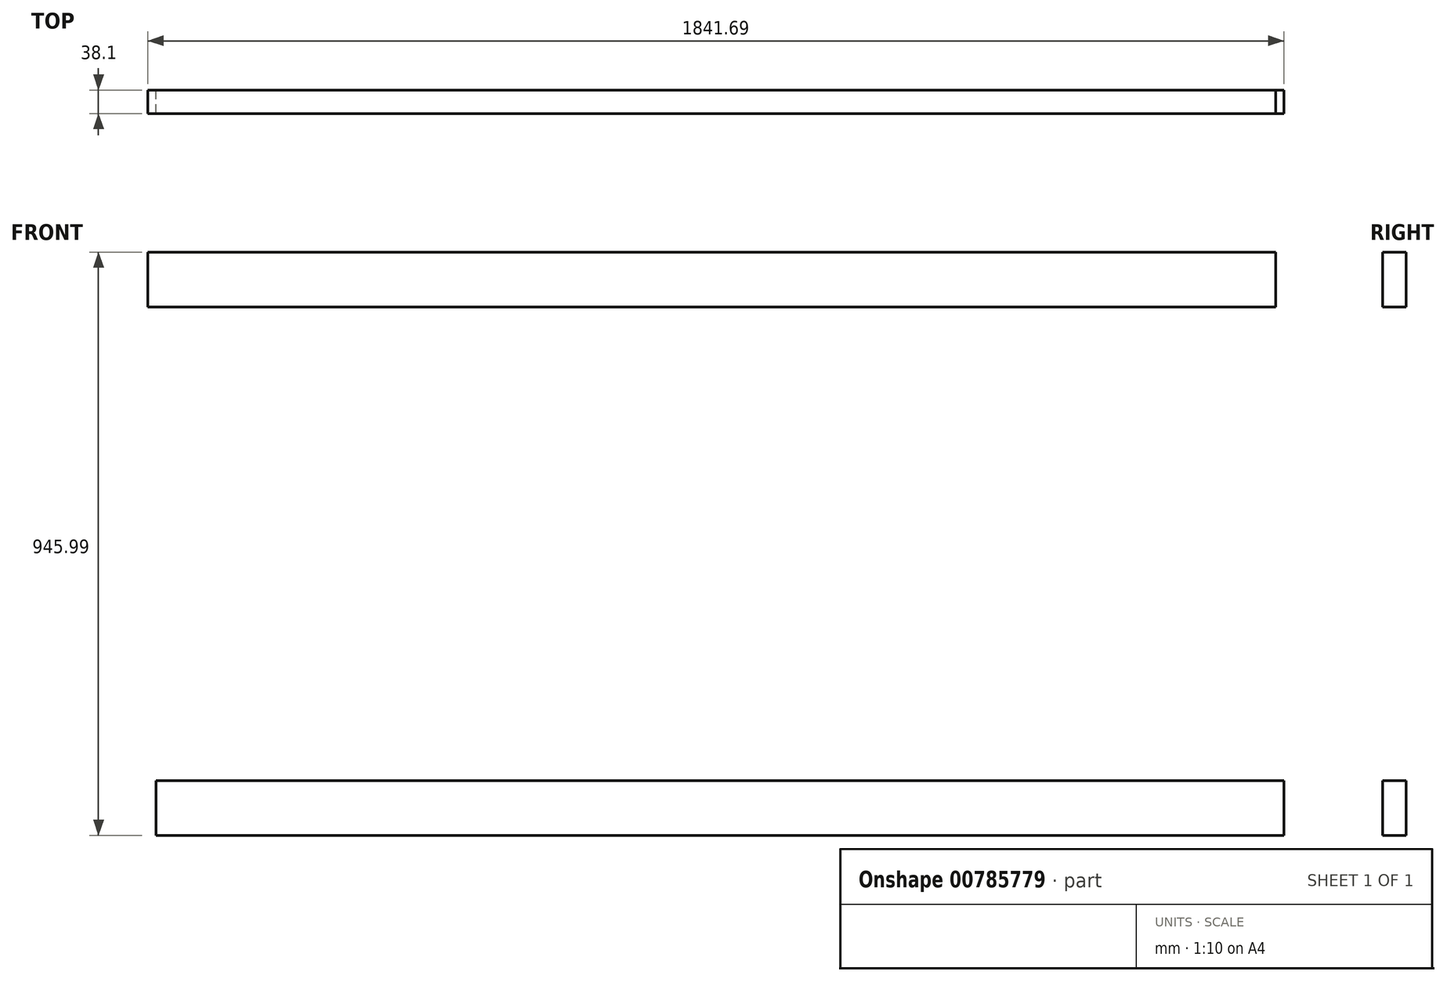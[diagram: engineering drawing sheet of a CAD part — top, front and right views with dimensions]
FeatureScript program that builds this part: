
annotation { "Feature Type Name" : "Feature", "Feature Type Description" : "" }
export const myFeature = defineFeature(function(context is Context, id is Id, definition is map)
    precondition{}
    {
        {
            var Q0;
            Q0=qCreatedBy(makeId("Front.planeOp"),FACE);
            var sketch = newSketch(context, id + "F0", { "sketchPlane" : qUnion([Q0])});
            skLineSegment(sketch, "E0.bottom", {"start": v(-1030.42, 91.8) * mm, "end": v(798.38, 91.8) * mm});
            skLineSegment(sketch, "E0.top", {"start": v(-1030.42, 2.9) * mm, "end": v(798.38, 2.9) * mm});
            skLineSegment(sketch, "E0.left", {"start": v(-1030.42, 91.8) * mm, "end": v(-1030.42, 2.9) * mm});
            skLineSegment(sketch, "E0.right", {"start": v(798.38, 91.8) * mm, "end": v(798.38, 2.9) * mm});
            skLineSegment(sketch, "E1", {"start": v(-420.82, -44.14) * mm, "end": v(-420.82, 237.94) * mm, "construction": true});
            skLineSegment(sketch, "E2", {"start": v(-954.22, -38.98) * mm, "end": v(-954.22, 210.32) * mm, "construction": true});
            skLineSegment(sketch, "E3", {"start": v(-438.2, -512.5) * mm, "end": v(-438.2, -174.64) * mm, "construction": true});
            skLineSegment(sketch, "E4.bottom", {"start": v(-1017.53, -765.3) * mm, "end": v(811.27, -765.3) * mm});
            skLineSegment(sketch, "E4.top", {"start": v(-1017.53, -854.2) * mm, "end": v(811.27, -854.2) * mm});
            skLineSegment(sketch, "E4.right", {"start": v(811.27, -765.3) * mm, "end": v(811.27, -854.2) * mm});
            skLineSegment(sketch, "E5", {"start": v(-1017.53, -854.2) * mm, "end": v(-1017.53, -765.3) * mm});
            skLineSegment(sketch, "E6", {"start": v(277.87, -1044.99) * mm, "end": v(277.87, -631.6) * mm, "construction": true});
            skLineSegment(sketch, "E7", {"start": v(-26.93, -1013.19) * mm, "end": v(-26.93, -671.35) * mm, "construction": true});
            skLineSegment(sketch, "E8", {"start": v(-331.73, -650.5) * mm, "end": v(-331.73, -1024.86) * mm, "construction": true});
            skSolve(sketch);
        }
        {
            var Q0;
            Q0=makeQuery(id+"F0.imprint","IMPRINT",FACE,{"disambiguationData":[TD([[makeQuery(id+"F0.imprint","IMPRINT",EDGE,{"derivedFrom":sQuery(id+"F0.wireOp",EDGE,"E0.bottom")}),-1.0]])]});
            var Q1;
            Q1=makeQuery(id+"F0.imprint","IMPRINT",FACE,{"disambiguationData":[TD([[makeQuery(id+"F0.imprint","IMPRINT",EDGE,{"derivedFrom":sQuery(id+"F0.wireOp",EDGE,"E4.bottom")}),-1.0]])]});
            extrude(context, id + "F1", {"entities" : qUnion([Q0, Q1]), "depth" : 38.1 * mm, "offsetDistance" : 25.4 * mm});
        }
    });
